# Revit family: 101010001058001
name_source: partatom
category: Modelos genéricos
revit_build: Autodesk Revit 2018 (Build: 20190510_1515(x64)
units: mm (PartAtom-declared; Revit-internal decimal feet)

## family parameters
Compartido = No
Corte con vacíos al cargar = No
Cota de conector redondo = Diámetro de uso
Puede alojar armadura = No
Punto de cálculo de habitación = No
Se basa en plano de trabajo = No
Siempre vertical = No
Tipo de pieza = Normal

## types (1)
- ESQUINERO DE MOLDAJE PVC 40X20X15MM BLANCO TIRA 3MT
    Aplicacion = Se utilizan para biselar los cantos de pilares y losas.
    Color = Blanco o Café
    Descripción = Se utilizan para biselar los cantos de pilares y losas.
    Dimension = 40 mm  [stored 0.131234 ft]
    Dureza = Shore A 70
    Empresa = CNP SPA.
    Espesor = 15 mm  [stored 0.0492126 ft]
    Largo = 3000 mm  [stored 9.84252 ft]
    Material = PVC flexible blanco
    Modelo = ESQUINERO DE MOLDAJE 40X20X15MM
    Nombre SKU = ESQUINERO DE MOLDAJE PVC 40X20X15MM BLANCO TIRA 3MT
    Num SKUs = 101010001058001
    URL = https://www.empresascnp.cl
    Unidad = Tira 3.00 mts.
    Url Ficha tecnica = https://empresascnp.cl
    Uso = Se utilizan para biselar los cantos de pilares y losas. Se aplican en forma horizontal y vertical al interior del
encofrado o placa fenólica. Es un producto fácil de
instalar, al ser semi-rígido permite varios usos, ahorro en
mano de obre para retoques de esquinas.
    Ventajas = Autoextinguible

note: [stored X ft] marks values corroborated as IEEE doubles in the binary element streams (Revit-internal decimal feet)

## geometry (parser evidence)
native form markers: Sweep x2
no freeform markers — native parametric forms only
